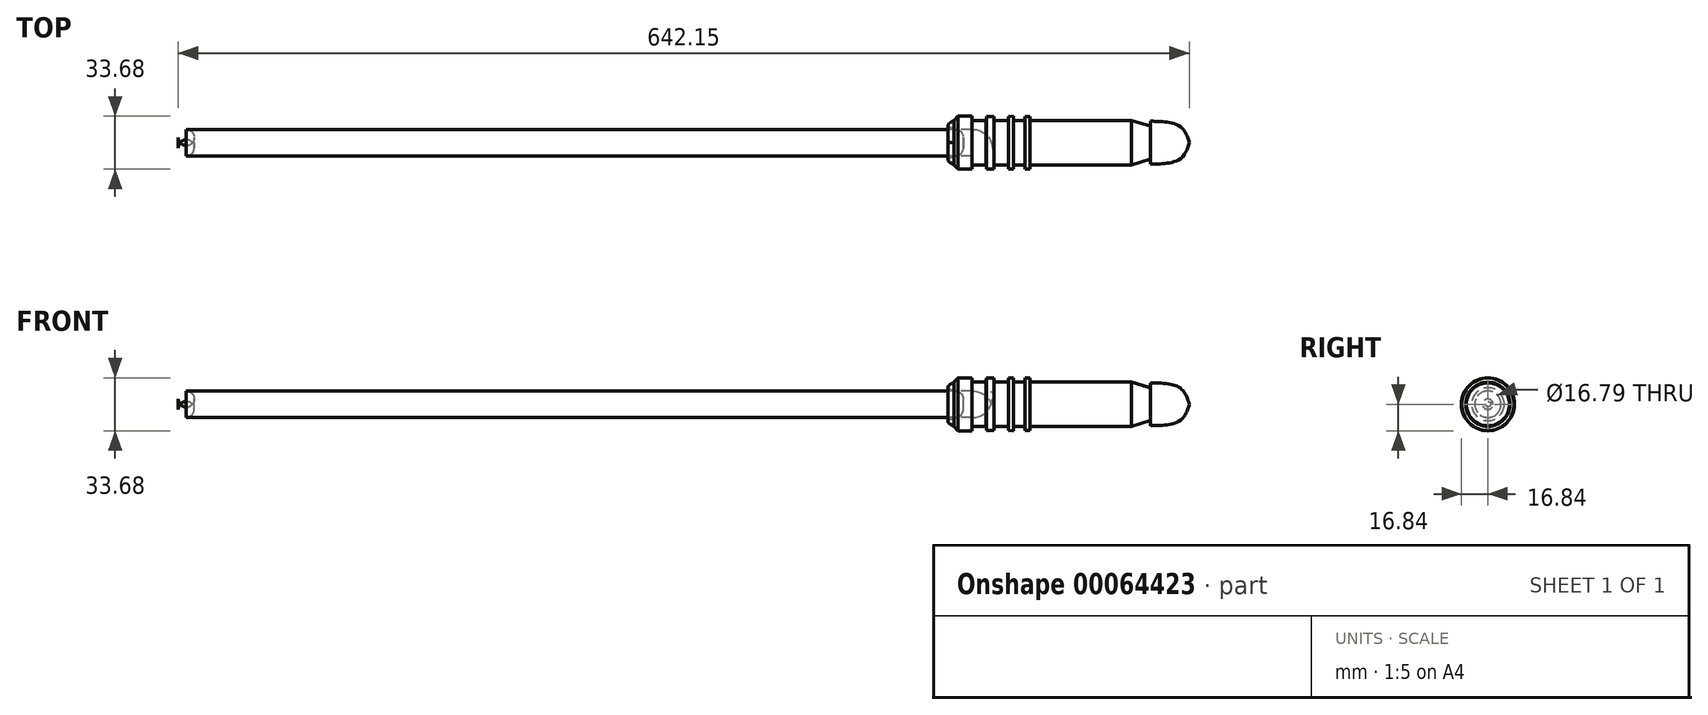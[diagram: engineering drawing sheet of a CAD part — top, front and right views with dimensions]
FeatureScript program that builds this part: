
annotation { "Feature Type Name" : "Feature", "Feature Type Description" : "" }
export const myFeature = defineFeature(function(context is Context, id is Id, definition is map)
    precondition{}
    {
        {
            var Q0;
            Q0=qCreatedBy(makeId("Front.planeOp"),FACE);
            var sketch = newSketch(context, id + "F0", { "sketchPlane" : qUnion([Q0])});
            skLineSegment(sketch, "E0", {"start": v(-58.49, 0) * mm, "end": v(67.3, 0) * mm});
            skFitSpline(sketch, "E1", {"points": [v(67.3, 0) * mm, v(61.35, 10.42) * mm, v(42.58, 13.62) * mm], "startDerivative": vector(-8.98, 27.48) * mm, "endDerivative": vector(-39.3, 0.79) * mm});
            skLineSegment(sketch, "E2", {"start": v(42.58, 13.62) * mm, "end": v(42.58, 10.42) * mm});
            skLineSegment(sketch, "E3", {"start": v(42.58, 10.42) * mm, "end": v(30.68, 14.08) * mm});
            skLineSegment(sketch, "E4", {"start": v(30.68, 14.08) * mm, "end": v(-82.18, 14.08) * mm});
            skFitSpline(sketch, "E5", {"points": [v(-82.18, 14.08) * mm, v(-86.08, 10.87) * mm, v(-82.18, 8.4) * mm], "startDerivative": vector(-11.73, -6.33) * mm, "endDerivative": vector(11.62, -7.4) * mm});
            skLineSegment(sketch, "E6", {"start": v(-82.18, 8.4) * mm, "end": v(-70.28, 8.4) * mm});
            skArc(sketch, "E7", {"start": v(-58.49, 0) * mm, "mid": v(-63.04, 6.08) * mm, "end": v(-70.28, 8.4) * mm});
            skLineSegment(sketch, "E8", {"start": v(-47.58, 14.08) * mm, "end": v(-47.58, 16.63) * mm});
            skLineSegment(sketch, "E9", {"start": v(-47.58, 16.63) * mm, "end": v(-44.34, 14.08) * mm});
            skLineSegment(sketch, "E10", {"start": v(-44.34, 14.08) * mm, "end": v(-44.34, 16.84) * mm});
            skLineSegment(sketch, "E11", {"start": v(-44.34, 16.84) * mm, "end": v(-47.58, 16.63) * mm});
            skLineSegment(sketch, "E12", {"start": v(-61.62, 16.63) * mm, "end": v(-56.65, 16.63) * mm});
            skLineSegment(sketch, "E13", {"start": v(-56.65, 16.63) * mm, "end": v(-56.65, 14.08) * mm});
            skLineSegment(sketch, "E14", {"start": v(-56.65, 14.08) * mm, "end": v(-61.84, 14.08) * mm});
            skLineSegment(sketch, "E15", {"start": v(-61.84, 14.08) * mm, "end": v(-61.62, 16.63) * mm});
            skLineSegment(sketch, "E16", {"start": v(-37.2, 14.08) * mm, "end": v(-37.2, 16.63) * mm});
            skLineSegment(sketch, "E17", {"start": v(-37.2, 16.63) * mm, "end": v(-33.97, 16.63) * mm});
            skLineSegment(sketch, "E18", {"start": v(-33.97, 16.63) * mm, "end": v(-33.97, 14.08) * mm});
            skLineSegment(sketch, "E19", {"start": v(-82.18, 14.08) * mm, "end": v(-79.78, 16.84) * mm});
            skLineSegment(sketch, "E20", {"start": v(-79.78, 16.84) * mm, "end": v(-70.7, 16.84) * mm});
            skLineSegment(sketch, "E21", {"start": v(-70.7, 16.84) * mm, "end": v(-70.7, 14.08) * mm});
            skSolve(sketch);
        }
        {
            var Q0;
            Q0 = qSketchRegion(id + "F0", true);
            var Q1;
            Q1=sQuery(id+"F0.wireOp",EDGE,"E0");
            revolve(context, id + "F1", {"entities" : qUnion([Q0]), "axis" : qUnion([Q1]), "revolveType" : RevolveType.FULL});
        }
        {
            var Q0;
            Q0=qCreatedBy(makeId("Right.planeOp"),FACE);
            cPlane(context, id + "F2", {"entities" : qUnion([Q0]), "cplaneType" : CPlaneType.OFFSET, "offset" : 76.2 * mm, "oppositeDirection" : true, "width" : 152.4 * mm, "height" : 152.4 * mm});
        }
        {
            var Q0;
            Q0=qCreatedBy(id+"F2.planeOp",FACE);
            var sketch = newSketch(context, id + "F3", { "sketchPlane" : qUnion([Q0])});
            skCircle(sketch, "E22", {"center": v(0, 0) * mm, "radius": 8.37 * mm});
            skSolve(sketch);
        }
        {
            var Q0;
            Q0=qCreatedBy(makeId("Front.planeOp"),FACE);
            var sketch = newSketch(context, id + "F4", { "sketchPlane" : qUnion([Q0])});
            skLineSegment(sketch, "E23", {"start": v(-76.45, 0) * mm, "end": v(-258.48, 0) * mm});
            skLineSegment(sketch, "E24", {"start": v(-258.48, 0) * mm, "end": v(-575.1, 0) * mm});
            skSolve(sketch);
        }
        {
            var Q0;
            Q0 = qSketchRegion(id + "F3", true);
            var Q1;
            Q1 = qConstructionFilter(qBodyType(qCreatedBy(id + "F4" ,EDGE), BodyType.WIRE), ConstructionObject.NO);
            sweep(context, id + "F5", {"profiles" : qUnion([Q0]), "path" : qUnion([Q1])});
        }
        {
            var Q0;
            Q0=makeQuery(id+"F5.opSweep","SWEPT_FACE",FACE,{"disambiguationData":[OSD([sQuery(id+"F3.wireOp",EDGE,"E22"),sQuery(id+"F4.wireOp",EDGE,"E23")])]});
            fillet(context, id + "F6", {"entities" : qUnion([Q0]), "radius" : 5.08 * mm, "tangentPropagation" : true, "allowEdgeOverflow" : false});
        }
    });
